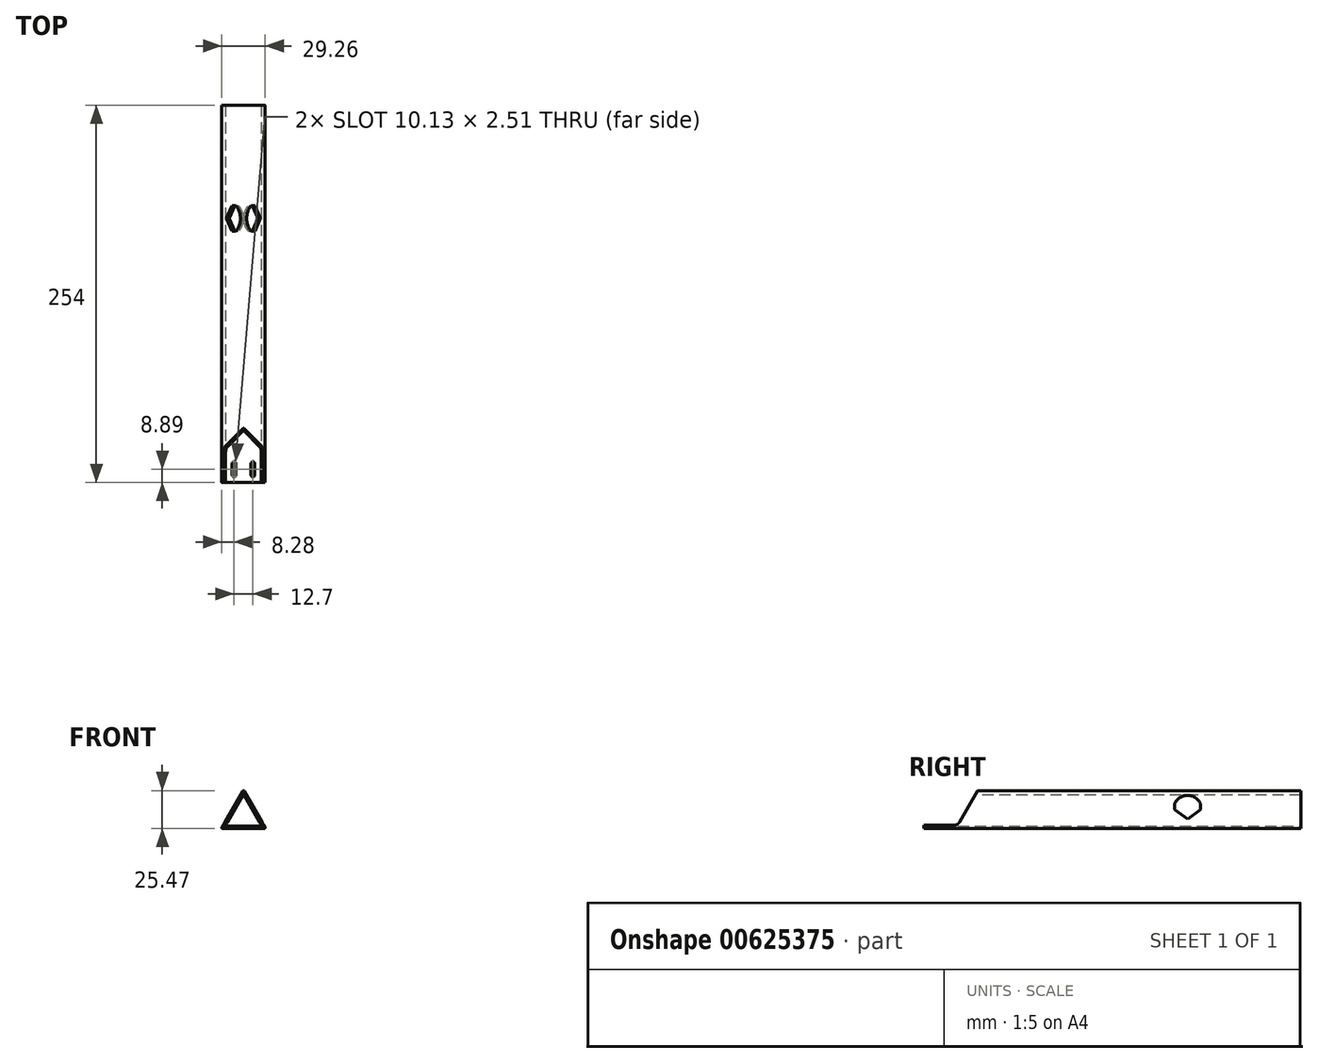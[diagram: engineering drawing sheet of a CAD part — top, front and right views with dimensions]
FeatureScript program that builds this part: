
annotation { "Feature Type Name" : "Feature", "Feature Type Description" : "" }
export const myFeature = defineFeature(function(context is Context, id is Id, definition is map)
    precondition{}
    {
        {
            var Q0;
            Q0=qCreatedBy(makeId("Front.planeOp"),FACE);
            var sketch = newSketch(context, id + "F0", { "sketchPlane" : qUnion([Q0])});
            skLineSegment(sketch, "E0", {"start": v(-15, 0) * mm, "end": v(15, 0) * mm});
            skLineSegment(sketch, "E1", {"start": v(15, 0) * mm, "end": v(0, 25.98) * mm});
            skLineSegment(sketch, "E2", {"start": v(0, 25.98) * mm, "end": v(-15, 0) * mm});
            skLineSegment(sketch, "E3", {"start": v(0, 22.98) * mm, "end": v(-12.4, 1.5) * mm});
            skLineSegment(sketch, "E4", {"start": v(-12.4, 1.5) * mm, "end": v(12.4, 1.5) * mm});
            skLineSegment(sketch, "E5", {"start": v(12.4, 1.5) * mm, "end": v(0, 22.98) * mm});
            skLineSegment(sketch, "E6", {"start": v(3.26, 17.34) * mm, "end": v(4.56, 18.1) * mm, "construction": true});
            skLineSegment(sketch, "E7", {"start": v(5, 1.5) * mm, "end": v(5, 0) * mm, "construction": true});
            skLineSegment(sketch, "E8", {"start": v(-4.44, 15.3) * mm, "end": v(-5.74, 16.05) * mm, "construction": true});
            skSolve(sketch);
        }
        {
            var Q0;
            Q0 = qSketchRegion(id + "F0", true);
            extrude(context, id + "F1", {"entities" : qUnion([Q0]), "depth" : 177.8 * mm, "offsetDistance" : 25.4 * mm, "hasSecondDirection" : true, "secondDirectionOppositeDirection" : true, "secondDirectionDepth" : 76.2 * mm});
        }
        {
            var Q0;
            Q0=makeQuery(id+"F1.opExtrude","SWEPT_EDGE",EDGE,{"disambiguationData":[OSD([sQuery(id+"F0.wireOp",EDGE,"E1"),sQuery(id+"F0.wireOp",EDGE,"E2")])]});
            var Q1;
            Q1=makeQuery(id+"F1.opExtrude","SWEPT_EDGE",EDGE,{"disambiguationData":[OSD([sQuery(id+"F0.wireOp",EDGE,"E0"),sQuery(id+"F0.wireOp",EDGE,"E1")])]});
            var Q2;
            Q2=makeQuery(id+"F1.opExtrude","SWEPT_EDGE",EDGE,{"disambiguationData":[OSD([sQuery(id+"F0.wireOp",EDGE,"E0"),sQuery(id+"F0.wireOp",EDGE,"E2")])]});
            var Q3;
            Q3=makeQuery(id+"F1.opExtrude","SWEPT_EDGE",EDGE,{"disambiguationData":[OSD([sQuery(id+"F0.wireOp",EDGE,"E3"),sQuery(id+"F0.wireOp",EDGE,"E4")])]});
            var Q4;
            Q4=makeQuery(id+"F1.opExtrude","SWEPT_EDGE",EDGE,{"disambiguationData":[OSD([sQuery(id+"F0.wireOp",EDGE,"E3"),sQuery(id+"F0.wireOp",EDGE,"E5")])]});
            var Q5;
            Q5=makeQuery(id+"F1.opExtrude","SWEPT_EDGE",EDGE,{"disambiguationData":[OSD([sQuery(id+"F0.wireOp",EDGE,"E4"),sQuery(id+"F0.wireOp",EDGE,"E5")])]});
            fillet(context, id + "F2", {"entities" : qUnion([Q0, Q1, Q2, Q3, Q4, Q5]), "radius" : 0.5 * mm, "tangentPropagation" : true, "allowEdgeOverflow" : false});
        }
        {
            var Q0;
            Q0=qCreatedBy(makeId("Right.planeOp"),FACE);
            var sketch = newSketch(context, id + "F3", { "sketchPlane" : qUnion([Q0])});
            skCircle(sketch, "E9", {"center": v(0, 14.32) * mm, "radius": 6.5 * mm, "construction": true});
            skLineSegment(sketch, "E10", {"start": v(-8.67, 12.66) * mm, "end": v(0, 6.22) * mm});
            skLineSegment(sketch, "E11", {"start": v(0, 6.22) * mm, "end": v(8.67, 12.66) * mm});
            skLineSegment(sketch, "E12", {"start": v(8.67, 12.66) * mm, "end": v(8.67, 16.77) * mm});
            skLineSegment(sketch, "E13", {"start": v(-8.69, 16.77) * mm, "end": v(-8.67, 12.66) * mm});
            skArc(sketch, "E14", {"start": v(8.67, 16.77) * mm, "mid": v(0, 22.32) * mm, "end": v(-8.69, 16.77) * mm});
            skSolve(sketch);
        }
        {
            var Q0;
            Q0 = qSketchRegion(id + "F3", true);
            extrude(context, id + "F4", {"entities" : qUnion([Q0]), "operationType" : NewBodyOperationType.REMOVE, "endBound" : BoundingType.THROUGH_ALL, "oppositeDirection" : true, "depth" : 25.4 * mm, "offsetDistance" : 25.4 * mm, "hasSecondDirection" : true, "secondDirectionBound" : SecondDirectionBoundingType.THROUGH_ALL, "secondDirectionOppositeDirection" : false, "secondDirectionDepth" : 25.4 * mm});
        }
        {
            var Q0;
            Q0=qCreatedBy(makeId("Top.planeOp"),FACE);
            var sketch = newSketch(context, id + "F5", { "sketchPlane" : qUnion([Q0])});
            skArc(sketch, "E15", {"start": v(-5.1, -165.1) * mm, "mid": v(-6.35, -163.84) * mm, "end": v(-7.6, -165.1) * mm});
            skArc(sketch, "E16", {"start": v(-7.6, -172.72) * mm, "mid": v(-6.35, -173.98) * mm, "end": v(-5.1, -172.72) * mm});
            skLineSegment(sketch, "E17", {"start": v(-7.6, -165.1) * mm, "end": v(-7.6, -172.72) * mm});
            skLineSegment(sketch, "E18", {"start": v(-5.1, -165.1) * mm, "end": v(-5.1, -172.72) * mm});
            skLineSegment(sketch, "E19", {"start": v(0, 0) * mm, "end": v(0, -220.06) * mm, "construction": true});
            skArc(sketch, "E20.MirrorCS", {"start": v(5.1, -165.1) * mm, "mid": v(6.35, -163.84) * mm, "end": v(7.6, -165.1) * mm});
            skArc(sketch, "E21.MirrorCS", {"start": v(7.6, -172.72) * mm, "mid": v(6.35, -173.98) * mm, "end": v(5.1, -172.72) * mm});
            skLineSegment(sketch, "E22.MirrorCS", {"start": v(7.6, -165.1) * mm, "end": v(7.6, -172.72) * mm});
            skLineSegment(sketch, "E23.MirrorCS", {"start": v(5.1, -165.1) * mm, "end": v(5.1, -172.72) * mm});
            skSolve(sketch);
        }
        {
            var Q0;
            Q0 = qSketchRegion(id + "F5", true);
            extrude(context, id + "F6", {"entities" : qUnion([Q0]), "operationType" : NewBodyOperationType.REMOVE, "endBound" : BoundingType.THROUGH_ALL, "depth" : 25.4 * mm, "offsetDistance" : 25.4 * mm});
        }
        {
            var Q0;
            Q0=qCreatedBy(makeId("Right.planeOp"),FACE);
            var sketch = newSketch(context, id + "F7", { "sketchPlane" : qUnion([Q0])});
            skLineSegment(sketch, "E24", {"start": v(-205.74, 2.03) * mm, "end": v(-154.94, 2.03) * mm});
            skLineSegment(sketch, "E25", {"start": v(-154.94, 2.03) * mm, "end": v(-136.6, 33.78) * mm});
            skLineSegment(sketch, "E26", {"start": v(-136.6, 33.78) * mm, "end": v(-204.16, 33.78) * mm});
            skLineSegment(sketch, "E27", {"start": v(-204.16, 33.78) * mm, "end": v(-205.74, 2.03) * mm});
            skSolve(sketch);
        }
        {
            var Q0;
            Q0 = qSketchRegion(id + "F7", true);
            extrude(context, id + "F8", {"entities" : qUnion([Q0]), "operationType" : NewBodyOperationType.REMOVE, "endBound" : BoundingType.THROUGH_ALL, "oppositeDirection" : true, "depth" : 25.4 * mm, "offsetDistance" : 25.4 * mm, "hasSecondDirection" : true, "secondDirectionBound" : SecondDirectionBoundingType.THROUGH_ALL, "secondDirectionOppositeDirection" : false, "secondDirectionDepth" : 25.4 * mm});
        }
        {
            var Q0;
            {var subQ0=sQuery(id+"F7.wireOp",EDGE,"E24");var subQ1=sQuery(id+"F7.wireOp",EDGE,"E25");Q0=makeQuery(id+"F8.boolean.opBoolean","COPY",EDGE,{"disambiguationData":[TD([makeQuery(id+"F1.opExtrude","SWEPT_FACE",FACE,{"disambiguationData":[OSD([sQuery(id+"F0.wireOp",EDGE,"E1")])]})])],"derivedFrom":makeQuery(id+"F8.opExtrude","SWEPT_EDGE",EDGE,{"disambiguationData":[OSD([subQ0,subQ1])]})});}
            var Q1;
            {var subQ0=sQuery(id+"F7.wireOp",EDGE,"E25");var subQ1=sQuery(id+"F7.wireOp",EDGE,"E24");Q1=makeQuery(id+"F8.boolean.opBoolean","COPY",EDGE,{"disambiguationData":[TD([makeQuery(id+"F1.opExtrude","SWEPT_FACE",FACE,{"disambiguationData":[OSD([sQuery(id+"F0.wireOp",EDGE,"E2")])]})])],"derivedFrom":makeQuery(id+"F8.opExtrude","SWEPT_EDGE",EDGE,{"disambiguationData":[OSD([subQ1,subQ0])]})});}
            fillet(context, id + "F9", {"entities" : qUnion([Q0, Q1]), "radius" : 4.76 * mm, "tangentPropagation" : true, "allowEdgeOverflow" : false});
        }
    });
